# Revit family: Shower-Valve_Trim-KOHLER-Autosense-K-24431IN
name_source: partatom
category: Plumbing Fixtures
units: mm (PartAtom-declared; Revit-internal decimal feet)

## family parameters
Cut with Voids When Loaded = No
Host = Face
OmniClass Number = 23.31.17.00
OmniClass Title = Showers
Part Type = Normal
Room Calculation Point = No
Round Connector Dimension = Use Diameter
Shared = No

## types (6) — shared parameters
ADA Compliant = No
Assembly Code = D2010700
CW Connection = No
Cold Water Inlet = Cold Water Inlet
Date Modified = 01/25/2023
Default Elevation = 42"
Description = Th Rec B&S Universal Trim
Drain Included = No
Flow Rate = 0 GPM
HW Connection = No
Height = 7 1/16"
Hot Water Inlet = Hot Water Inlet
Length = 3 1/8"
Manufacturer = Kohler Co.
Master Format 2014 = 22 42 23
Master Format 2014 Name = Residential Showers
Material = Premium Metal Construction
Pressure = 0.00 psi
Product Name = Autosense
Product Page URL = https://www.kohler.co.in
URL = https://www.kohler.co.in
Vent Connection = No
Waste Connection = No
Waste Water Outlet = Waste Water Outlet
WaterSense Certified = No
Width = 5 1/2"

## per-type parameters (varying)
| type | Finish | Model | Type |
| AF-Vibrant French Gold | Kohler-Metal-AF-Vibrant_French_Gold | K-24431IN-9FP-AF | 1 |
| BL-Matte Black | Kohler-Metal-BL-Matte_Black | K-24431IN-9FP-BL | 2 |
| BN-Vibrant Brushed Nickel | Kohler-Metal-BN-Vibrant_Brushed_Nickel | K-24431IN-9FP-BN | 3 |
| BV-Brushed Bronze | Kohler-Metal-BV-Brushed_Bronze | K-24431IN-9FP-BV | 4 |
| CP-Polished Chrome | Kohler-Metal-CP-Polished_Chrome | K-24431IN-9FP-CP | 5 |
| RGD-Polished Rose Gold | Kohler-Metal-RGD-Polished_Rose_Gold | K-24431IN-9FP-RGD | 6 |

## geometry (parser evidence)
native form markers: Sweep x4
no freeform markers — native parametric forms only
